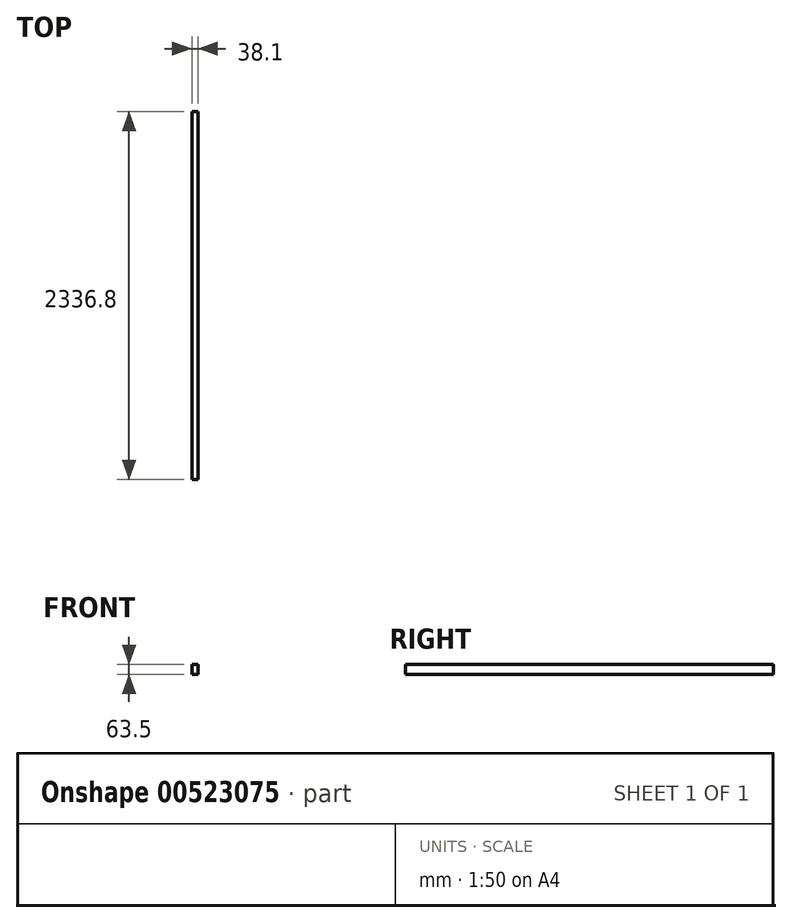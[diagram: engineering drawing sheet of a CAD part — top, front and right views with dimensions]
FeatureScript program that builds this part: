
annotation { "Feature Type Name" : "Feature", "Feature Type Description" : "" }
export const myFeature = defineFeature(function(context is Context, id is Id, definition is map)
    precondition{}
    {
        {
            var Q0;
            Q0=qCreatedBy(makeId("Front.planeOp"),FACE);
            var sketch = newSketch(context, id + "F0", { "sketchPlane" : qUnion([Q0])});
            skLineSegment(sketch, "E0.bottom", {"start": v(0, 0) * mm, "end": v(38.1, 0) * mm});
            skLineSegment(sketch, "E0.top", {"start": v(0, 63.5) * mm, "end": v(38.1, 63.5) * mm});
            skLineSegment(sketch, "E0.left", {"start": v(0, 0) * mm, "end": v(0, 63.5) * mm});
            skLineSegment(sketch, "E0.right", {"start": v(38.1, 0) * mm, "end": v(38.1, 63.5) * mm});
            skSolve(sketch);
        }
        {
            var Q0;
            Q0 = qSketchRegion(id + "F0", true);
            extrude(context, id + "F1", {"entities" : qUnion([Q0]), "depth" : 2336.8 * mm, "offsetDistance" : 25.4 * mm});
        }
    });
